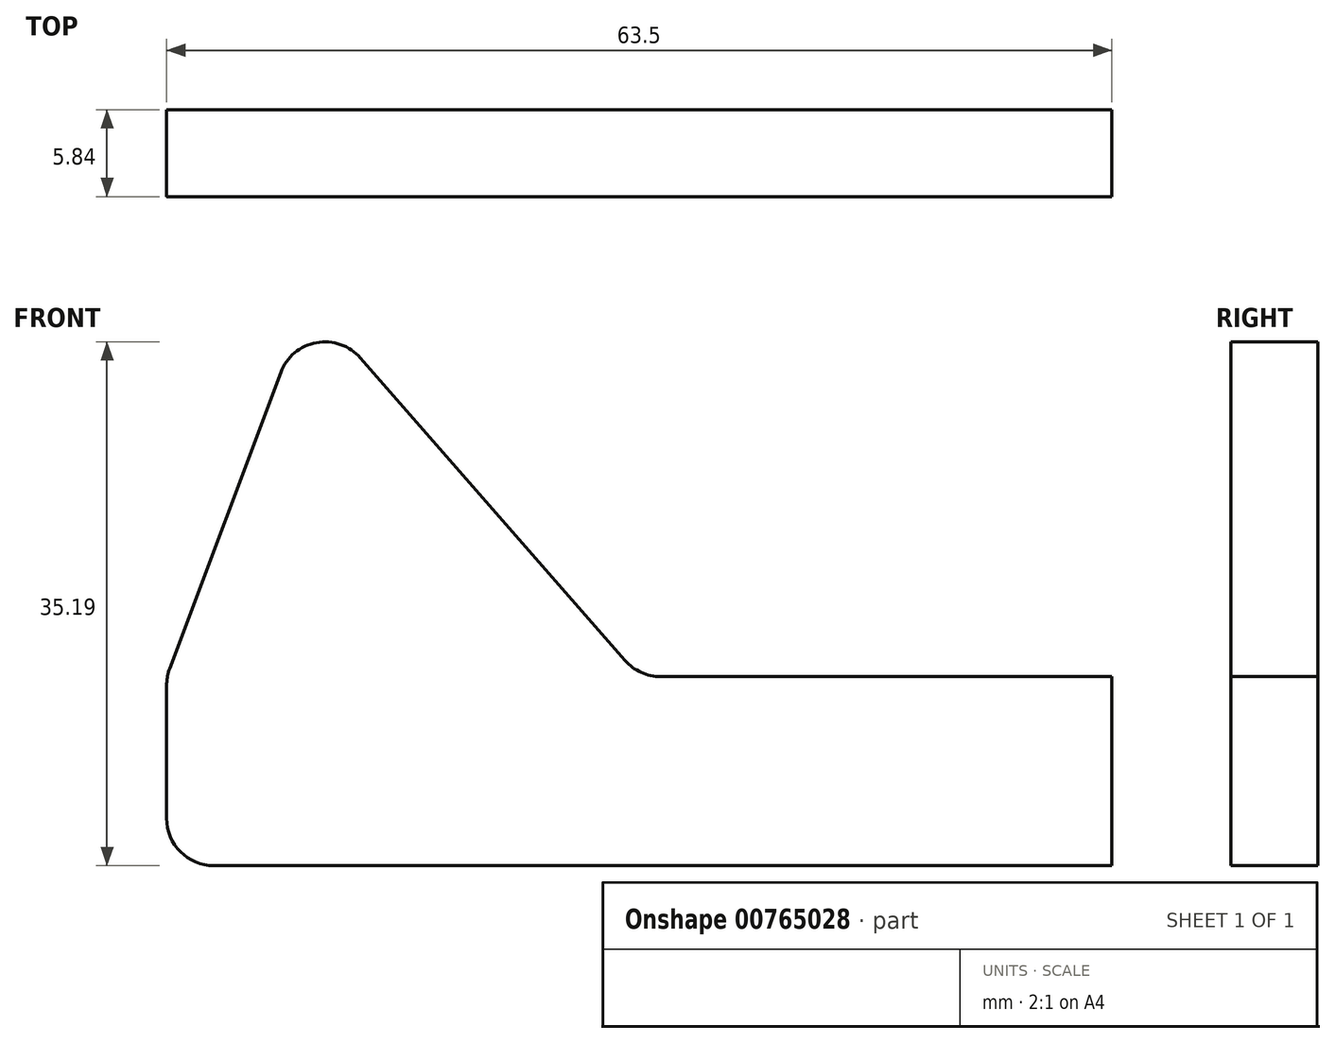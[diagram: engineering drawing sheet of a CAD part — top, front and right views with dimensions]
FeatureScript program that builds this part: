
annotation { "Feature Type Name" : "Feature", "Feature Type Description" : "" }
export const myFeature = defineFeature(function(context is Context, id is Id, definition is map)
    precondition{}
    {
        {
            var Q0;
            Q0=qCreatedBy(makeId("Front.planeOp"),FACE);
            var sketch = newSketch(context, id + "F0", { "sketchPlane" : qUnion([Q0])});
            skLineSegment(sketch, "E0.bottom", {"start": v(0, 6.35) * mm, "end": v(31.75, 6.35) * mm});
            skLineSegment(sketch, "E0.top", {"start": v(-31.75, -6.35) * mm, "end": v(31.75, -6.35) * mm});
            skLineSegment(sketch, "E0.left", {"start": v(-31.75, 6.35) * mm, "end": v(-31.75, -6.35) * mm});
            skLineSegment(sketch, "E0.right", {"start": v(31.75, 6.35) * mm, "end": v(31.75, -6.35) * mm});
            skPoint(sketch, "E0.middle", {"position": v(0, 0) * mm});
            skLineSegment(sketch, "E1", {"start": v(-31.75, 6.35) * mm, "end": v(-22.23, 31.75) * mm});
            skLineSegment(sketch, "E2", {"start": v(-22.23, 31.75) * mm, "end": v(0, 6.35) * mm});
            skSolve(sketch);
        }
        {
            var Q0;
            Q0 = qSketchRegion(id + "F0", true);
            extrude(context, id + "F1", {"entities" : qUnion([Q0]), "depth" : 5.84 * mm, "offsetDistance" : 25.4 * mm});
        }
        {
            var Q0;
            Q0=makeQuery(id+"F1.opExtrude","SWEPT_EDGE",EDGE,{"disambiguationData":[OSD([sQuery(id+"F0.wireOp",EDGE,"E0.bottom"),sQuery(id+"F0.wireOp",EDGE,"E2")])]});
            var Q1;
            Q1=makeQuery(id+"F1.opExtrude","SWEPT_EDGE",EDGE,{"disambiguationData":[OSD([sQuery(id+"F0.wireOp",EDGE,"E0.left"),sQuery(id+"F0.wireOp",EDGE,"E1")])]});
            var Q2;
            Q2=makeQuery(id+"F1.opExtrude","SWEPT_EDGE",EDGE,{"disambiguationData":[OSD([sQuery(id+"F0.wireOp",EDGE,"E0.top"),sQuery(id+"F0.wireOp",EDGE,"E0.left")])]});
            fillet(context, id + "F2", {"entities" : qUnion([Q0, Q1, Q2]), "radius" : 3.17 * mm, "tangentPropagation" : true, "allowEdgeOverflow" : false});
        }
        {
            var Q0;
            Q0=makeQuery(id+"F1.opExtrude","SWEPT_EDGE",EDGE,{"disambiguationData":[OSD([sQuery(id+"F0.wireOp",EDGE,"E1"),sQuery(id+"F0.wireOp",EDGE,"E2")])]});
            fillet(context, id + "F3", {"entities" : qUnion([Q0]), "radius" : 3.17 * mm, "tangentPropagation" : true, "allowEdgeOverflow" : false});
        }
    });
